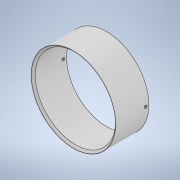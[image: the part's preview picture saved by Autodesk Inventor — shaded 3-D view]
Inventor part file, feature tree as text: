
AUTODESK INVENTOR PART (.ipt)
format: ipt  version: 2020.2 (Build 242310000, 310)  size: 264,192 bytes
history: native  units: mm
features: extrude x3, sketch x3, chamfer x1
ambient origin geometry x8: Origin, YZ Plane, XZ Plane, XY Plane, X Axis, Y Axis, Z Axis, Center Point
bodies: Solid1 (feature_tree)
feature tree (7):
  extrude  "Extrusion1"  Depth=1.0mm TaperAngle=45.0deg
  chamfer  "Chamfer1"  Distance=1.5mm
  extrude  "Extrusion2"  Depth=41.55mm
  extrude  "Extrusion3"  [1 undecoded]
  sketch  "Sketch1"  dims[d1=17.8mm d2=0.0mm d3=1.0mm d4=2.0mm d5=45.0deg d6=1.5mm d7=0.0mm]
  sketch  "Sketch2"  dims[d9=1.096917mm d10=41.55mm]
  sketch  "Sketch3"  dims[d11=100.0mm d12=0.0mm]
note: 1 required parameter value undecoded (feature->parameter linkage not recoverable at this tier; creation-order binding heuristic only, values carry confidence <= 0.55)
